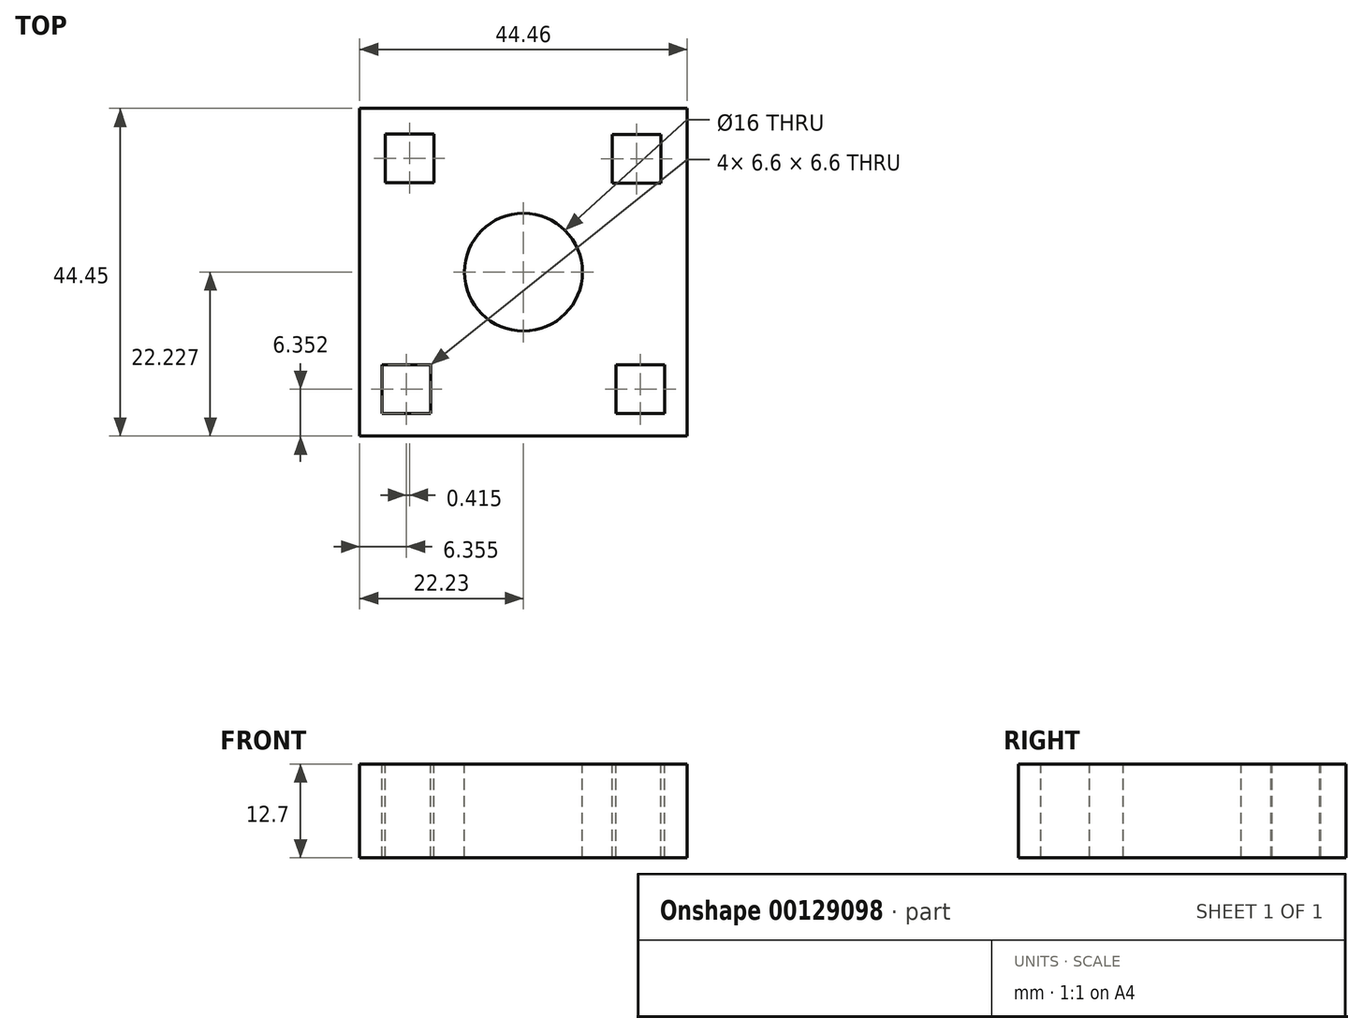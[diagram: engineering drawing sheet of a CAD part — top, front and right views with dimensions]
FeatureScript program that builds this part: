
annotation { "Feature Type Name" : "Feature", "Feature Type Description" : "" }
export const myFeature = defineFeature(function(context is Context, id is Id, definition is map)
    precondition{}
    {
        {
            var Q0;
            Q0=qCreatedBy(makeId("Top.planeOp"),FACE);
            var sketch = newSketch(context, id + "F0", { "sketchPlane" : qUnion([Q0])});
            skLineSegment(sketch, "E0.bottom", {"start": v(-22.23, 37.82) * mm, "end": v(22.23, 37.82) * mm});
            skLineSegment(sketch, "E0.top", {"start": v(-22.23, -6.63) * mm, "end": v(22.23, -6.63) * mm});
            skLineSegment(sketch, "E0.left", {"start": v(-22.23, 37.82) * mm, "end": v(-22.23, -6.63) * mm});
            skLineSegment(sketch, "E0.right", {"start": v(22.23, 37.82) * mm, "end": v(22.23, -6.63) * mm});
            skLineSegment(sketch, "E1", {"start": v(12.78, -6.63) * mm, "end": v(-5.28, -6.63) * mm});
            skLineSegment(sketch, "E2", {"start": v(0, 23.9) * mm, "end": v(0, 15.6) * mm, "construction": true});
            skSolve(sketch);
        }
        {
            var Q0;
            Q0 = qSketchRegion(id + "F0", true);
            extrude(context, id + "F1", {"entities" : qUnion([Q0]), "depth" : 12.7 * mm});
        }
        {
            var Q0;
            Q0=makeQuery(id+"F1.opExtrude","CAP_FACE",FACE,{"disambiguationData":[OSD([sQuery(id+"F0.wireOp",EDGE,"E0.bottom"),sQuery(id+"F0.wireOp",EDGE,"E0.top"),sQuery(id+"F0.wireOp",EDGE,"E0.left"),sQuery(id+"F0.wireOp",EDGE,"E0.right"),sQuery(id+"F0.wireOp",EDGE,"E1")])],"isStart":false});
            var sketch = newSketch(context, id + "F2", { "sketchPlane" : qUnion([Q0])});
            skLineSegment(sketch, "E3", {"start": v(-22.22, -6.63) * mm, "end": v(22.22, 37.82) * mm, "construction": true});
            skLineSegment(sketch, "E4", {"start": v(-22.22, 37.82) * mm, "end": v(22.22, -6.63) * mm, "construction": true});
            skCircle(sketch, "E5", {"center": v(0, 15.6) * mm, "radius": 8 * mm});
            skLineSegment(sketch, "E6.bottom", {"start": v(-22.22, -6.63) * mm, "end": v(-15.88, -6.63) * mm, "construction": true});
            skLineSegment(sketch, "E6.top", {"start": v(-22.23, -0.28) * mm, "end": v(-15.88, -0.28) * mm, "construction": true});
            skLineSegment(sketch, "E6.left", {"start": v(-22.22, -6.63) * mm, "end": v(-22.22, -0.28) * mm, "construction": true});
            skLineSegment(sketch, "E6.right", {"start": v(-15.88, -6.63) * mm, "end": v(-15.88, -0.28) * mm, "construction": true});
            skLineSegment(sketch, "E7.bottom", {"start": v(-22.22, 37.82) * mm, "end": v(-15.46, 37.82) * mm, "construction": true});
            skLineSegment(sketch, "E7.top", {"start": v(-22.23, 31.06) * mm, "end": v(-15.46, 31.06) * mm, "construction": true});
            skLineSegment(sketch, "E7.left", {"start": v(-22.22, 37.82) * mm, "end": v(-22.22, 31.06) * mm, "construction": true});
            skLineSegment(sketch, "E7.right", {"start": v(-15.46, 37.82) * mm, "end": v(-15.46, 31.06) * mm, "construction": true});
            skLineSegment(sketch, "E8.bottom", {"start": v(22.22, 37.82) * mm, "end": v(15.36, 37.82) * mm, "construction": true});
            skLineSegment(sketch, "E8.top", {"start": v(22.23, 30.95) * mm, "end": v(15.36, 30.95) * mm, "construction": true});
            skLineSegment(sketch, "E8.left", {"start": v(22.22, 37.82) * mm, "end": v(22.22, 30.95) * mm, "construction": true});
            skLineSegment(sketch, "E8.right", {"start": v(15.36, 37.82) * mm, "end": v(15.36, 30.95) * mm, "construction": true});
            skLineSegment(sketch, "E9.bottom", {"start": v(22.22, -6.63) * mm, "end": v(15.87, -6.63) * mm, "construction": true});
            skLineSegment(sketch, "E9.top", {"start": v(22.23, -0.28) * mm, "end": v(15.87, -0.28) * mm, "construction": true});
            skLineSegment(sketch, "E9.left", {"start": v(22.23, -6.63) * mm, "end": v(22.23, -0.28) * mm, "construction": true});
            skLineSegment(sketch, "E9.right", {"start": v(15.87, -6.63) * mm, "end": v(15.87, -0.28) * mm, "construction": true});
            skLineSegment(sketch, "E10.bottom", {"start": v(-12.16, 27.76) * mm, "end": v(-18.76, 27.76) * mm});
            skLineSegment(sketch, "E10.top", {"start": v(-12.16, 34.36) * mm, "end": v(-18.76, 34.36) * mm});
            skLineSegment(sketch, "E10.left", {"start": v(-12.16, 27.76) * mm, "end": v(-12.16, 34.36) * mm});
            skLineSegment(sketch, "E10.right", {"start": v(-18.76, 27.76) * mm, "end": v(-18.76, 34.36) * mm});
            skPoint(sketch, "E10.middle", {"position": v(-15.46, 31.06) * mm});
            skLineSegment(sketch, "E11.bottom", {"start": v(18.66, 27.65) * mm, "end": v(12.05, 27.65) * mm});
            skLineSegment(sketch, "E11.top", {"start": v(18.66, 34.25) * mm, "end": v(12.05, 34.25) * mm});
            skLineSegment(sketch, "E11.left", {"start": v(18.66, 27.65) * mm, "end": v(18.66, 34.25) * mm});
            skLineSegment(sketch, "E11.right", {"start": v(12.05, 27.65) * mm, "end": v(12.05, 34.25) * mm});
            skPoint(sketch, "E11.middle", {"position": v(15.36, 30.95) * mm});
            skLineSegment(sketch, "E12.bottom", {"start": v(12.57, 3.02) * mm, "end": v(19.18, 3.02) * mm});
            skLineSegment(sketch, "E12.top", {"start": v(12.57, -3.58) * mm, "end": v(19.18, -3.58) * mm});
            skLineSegment(sketch, "E12.left", {"start": v(12.57, 3.02) * mm, "end": v(12.57, -3.58) * mm});
            skLineSegment(sketch, "E12.right", {"start": v(19.18, 3.02) * mm, "end": v(19.18, -3.58) * mm});
            skPoint(sketch, "E12.middle", {"position": v(15.87, -0.28) * mm});
            skLineSegment(sketch, "E13.bottom", {"start": v(-12.57, -3.58) * mm, "end": v(-19.18, -3.58) * mm});
            skLineSegment(sketch, "E13.top", {"start": v(-12.57, 3.02) * mm, "end": v(-19.18, 3.02) * mm});
            skLineSegment(sketch, "E13.left", {"start": v(-12.57, -3.58) * mm, "end": v(-12.57, 3.02) * mm});
            skLineSegment(sketch, "E13.right", {"start": v(-19.18, -3.58) * mm, "end": v(-19.18, 3.02) * mm});
            skPoint(sketch, "E13.middle", {"position": v(-15.88, -0.28) * mm});
            skSolve(sketch);
        }
        {
            var Q0;
            Q0 = qSketchRegion(id + "F2", true);
            extrude(context, id + "F3", {"entities" : qUnion([Q0]), "operationType" : NewBodyOperationType.REMOVE, "oppositeDirection" : true, "depth" : 12.7 * mm});
        }
    });
